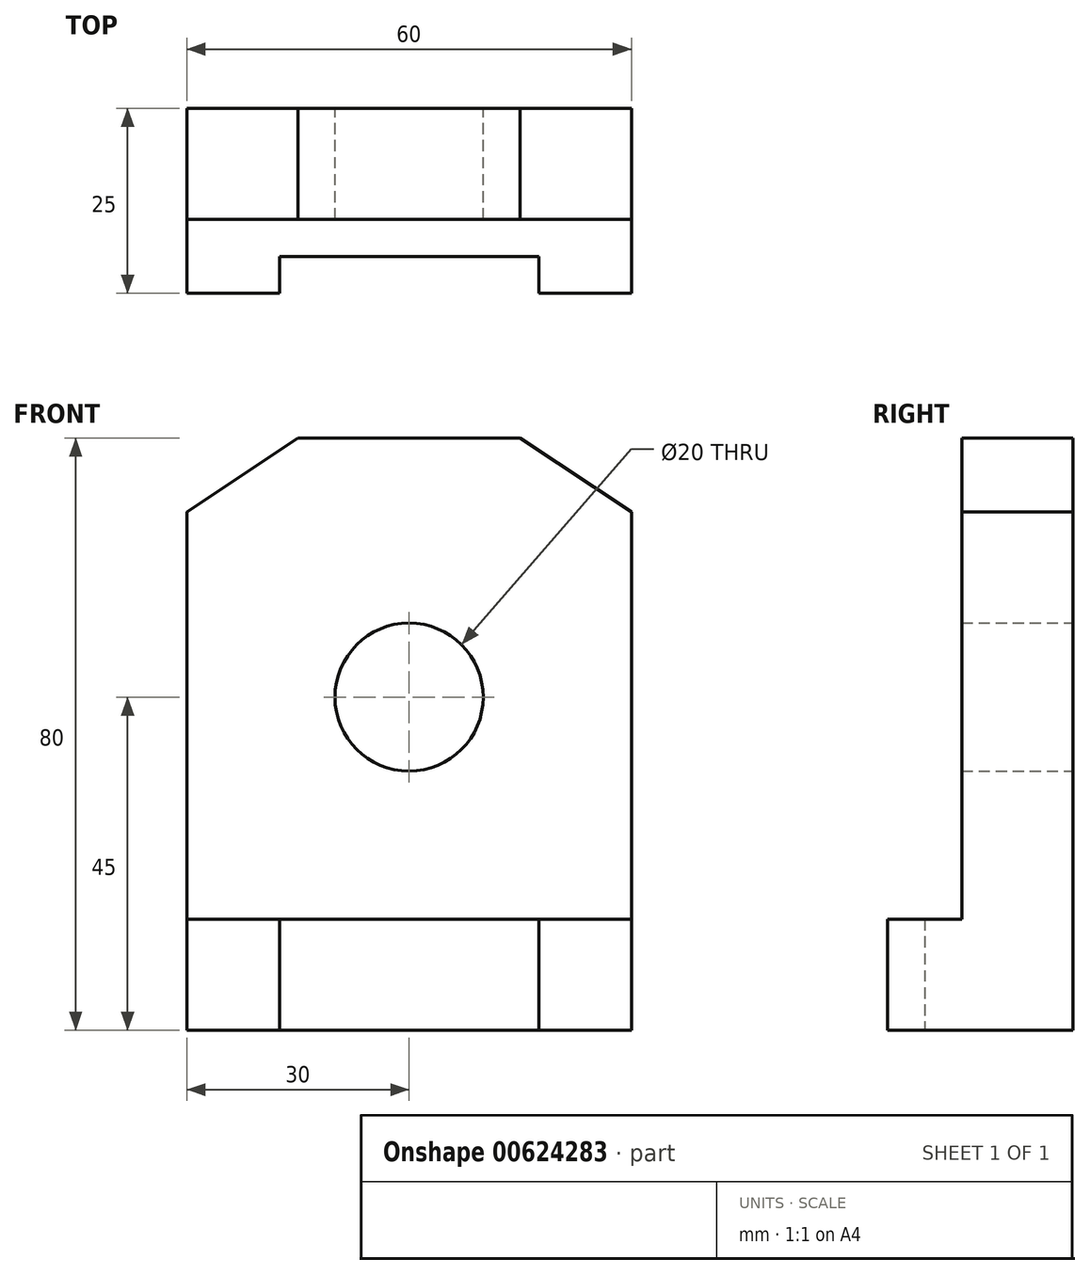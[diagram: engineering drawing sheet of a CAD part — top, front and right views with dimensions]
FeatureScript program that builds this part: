
annotation { "Feature Type Name" : "Feature", "Feature Type Description" : "" }
export const myFeature = defineFeature(function(context is Context, id is Id, definition is map)
    precondition{}
    {
        {
            var Q0;
            Q0=qCreatedBy(makeId("Front.planeOp"),FACE);
            var sketch = newSketch(context, id + "F0", { "sketchPlane" : qUnion([Q0])});
            skLineSegment(sketch, "E0", {"start": v(30, 0) * mm, "end": v(30, 70) * mm});
            skLineSegment(sketch, "E1", {"start": v(30, 70) * mm, "end": v(15, 80) * mm});
            skLineSegment(sketch, "E2", {"start": v(15, 80) * mm, "end": v(-15, 80) * mm});
            skLineSegment(sketch, "E3", {"start": v(-15, 80) * mm, "end": v(-30, 70) * mm});
            skLineSegment(sketch, "E4", {"start": v(-30, 70) * mm, "end": v(-30, 0) * mm});
            skLineSegment(sketch, "E5", {"start": v(-30, 0) * mm, "end": v(30, 0) * mm});
            skCircle(sketch, "E6", {"center": v(0, 45) * mm, "radius": 10 * mm});
            skSolve(sketch);
        }
        {
            var Q0;
            Q0=makeQuery(id+"F0.imprint","IMPRINT",FACE,{"disambiguationData":[TD([[makeQuery(id+"F0.imprint","IMPRINT",EDGE,{"derivedFrom":sQuery(id+"F0.wireOp",EDGE,"E0")}),1.0]])]});
            extrude(context, id + "F1", {"entities" : qUnion([Q0]), "depth" : 25 * mm, "offsetDistance" : 25 * mm});
        }
        {
            var Q0;
            Q0=makeQuery(id+"F1.opExtrude","SWEPT_FACE",FACE,{"disambiguationData":[OSD([sQuery(id+"F0.wireOp",EDGE,"E2")])]});
            var sketch = newSketch(context, id + "F2", { "sketchPlane" : qUnion([Q0])});
            skLineSegment(sketch, "E7", {"start": v(-15, -25) * mm, "end": v(30, -25) * mm});
            skLineSegment(sketch, "E8", {"start": v(30, -25) * mm, "end": v(30, -15) * mm});
            skLineSegment(sketch, "E9", {"start": v(30, -15) * mm, "end": v(-30, -15) * mm});
            skLineSegment(sketch, "E10", {"start": v(-30, -15) * mm, "end": v(-30, -25) * mm});
            skLineSegment(sketch, "E11", {"start": v(-30, -25) * mm, "end": v(-15, -25) * mm});
            skSolve(sketch);
        }
        {
            var Q0;
            Q0 = qSketchRegion(id + "F2", true);
            extrude(context, id + "F3", {"entities" : qUnion([Q0]), "operationType" : NewBodyOperationType.REMOVE, "oppositeDirection" : true, "depth" : 65 * mm, "offsetDistance" : 25 * mm});
        }
        {
            var Q0;
            Q0=qCreatedBy(makeId("Top.planeOp"),FACE);
            var sketch = newSketch(context, id + "F4", { "sketchPlane" : qUnion([Q0])});
            skLineSegment(sketch, "E12.bottom", {"start": v(17.5, -25) * mm, "end": v(-17.5, -25) * mm});
            skLineSegment(sketch, "E12.top", {"start": v(17.5, -20) * mm, "end": v(-17.5, -20) * mm});
            skLineSegment(sketch, "E12.left", {"start": v(17.5, -25) * mm, "end": v(17.5, -20) * mm});
            skPoint(sketch, "E12.middle", {"position": v(0, -22.5) * mm});
            skLineSegment(sketch, "E13", {"start": v(-17.5, -20) * mm, "end": v(-17.5, -25) * mm});
            skSolve(sketch);
        }
        {
            var Q0;
            Q0 = qSketchRegion(id + "F4", true);
            extrude(context, id + "F5", {"entities" : qUnion([Q0]), "operationType" : NewBodyOperationType.REMOVE, "depth" : 15 * mm, "offsetDistance" : 25 * mm});
        }
    });
